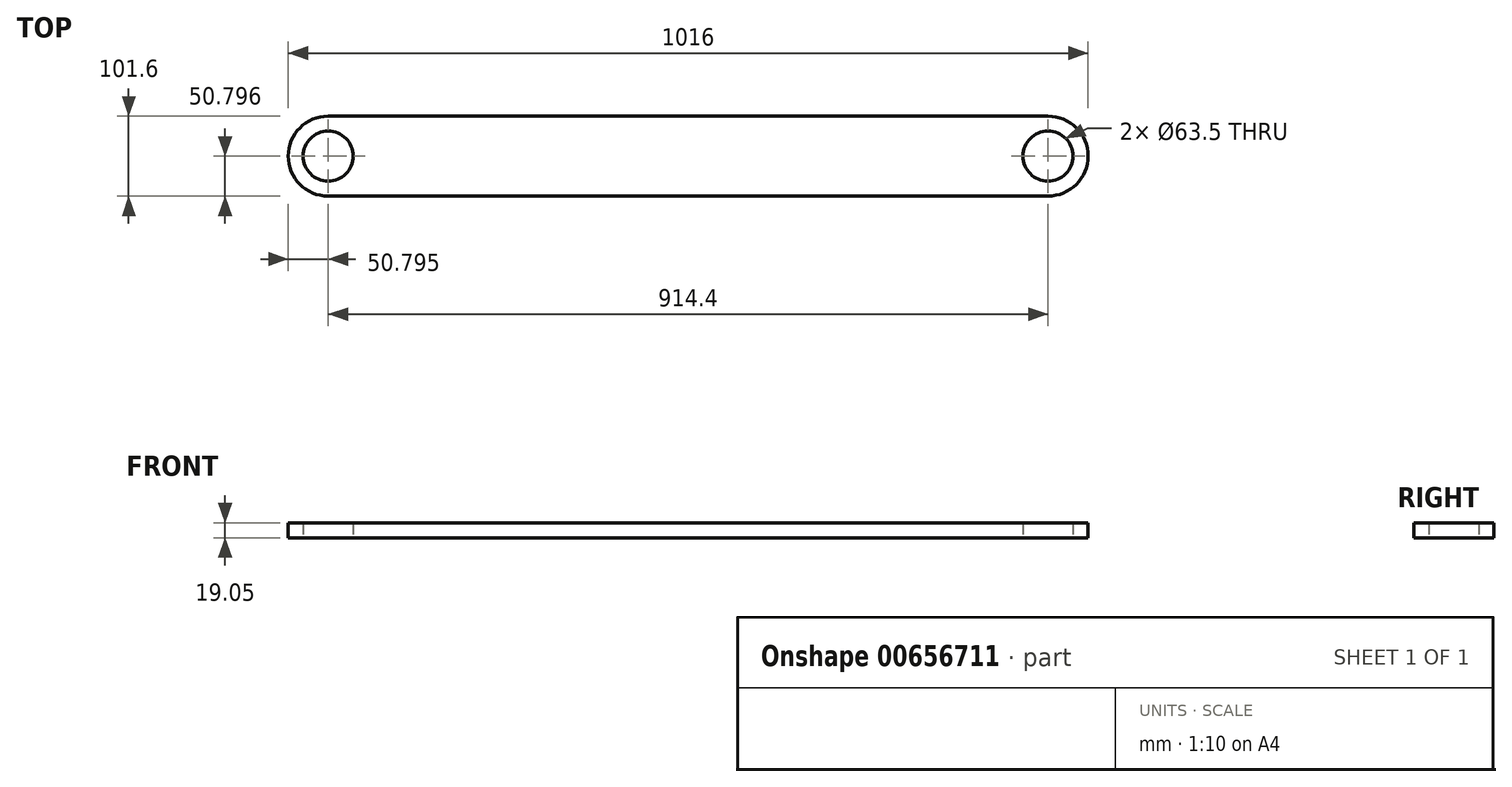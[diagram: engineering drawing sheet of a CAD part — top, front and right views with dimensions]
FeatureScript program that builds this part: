
annotation { "Feature Type Name" : "Feature", "Feature Type Description" : "" }
export const myFeature = defineFeature(function(context is Context, id is Id, definition is map)
    precondition{}
    {
        {
            var Q0;
            Q0=qCreatedBy(makeId("Top.planeOp"),FACE);
            var sketch = newSketch(context, id + "F0", { "sketchPlane" : qUnion([Q0])});
            skLineSegment(sketch, "E0.bottom", {"start": v(-972.6, 79.35) * mm, "end": v(-58.2, 79.35) * mm});
            skLineSegment(sketch, "E0.top", {"start": v(-972.6, -22.25) * mm, "end": v(-58.2, -22.25) * mm});
            skArc(sketch, "E1", {"start": v(-58.2, -22.25) * mm, "mid": v(-7.4, 28.55) * mm, "end": v(-58.2, 79.35) * mm});
            skArc(sketch, "E2", {"start": v(-972.6, 79.35) * mm, "mid": v(-1023.4, 28.55) * mm, "end": v(-972.6, -22.25) * mm});
            skCircle(sketch, "E3", {"center": v(-972.6, 28.55) * mm, "radius": 31.75 * mm});
            skCircle(sketch, "E4", {"center": v(-58.2, 28.55) * mm, "radius": 31.75 * mm});
            skSolve(sketch);
        }
        {
            var Q0;
            Q0=qSketchRegion(id+"F0",true);
            extrude(context, id + "F1", {"entities" : qUnion([Q0]), "depth" : 19.05 * mm, "offsetDistance" : 25.4 * mm});
        }
    });
